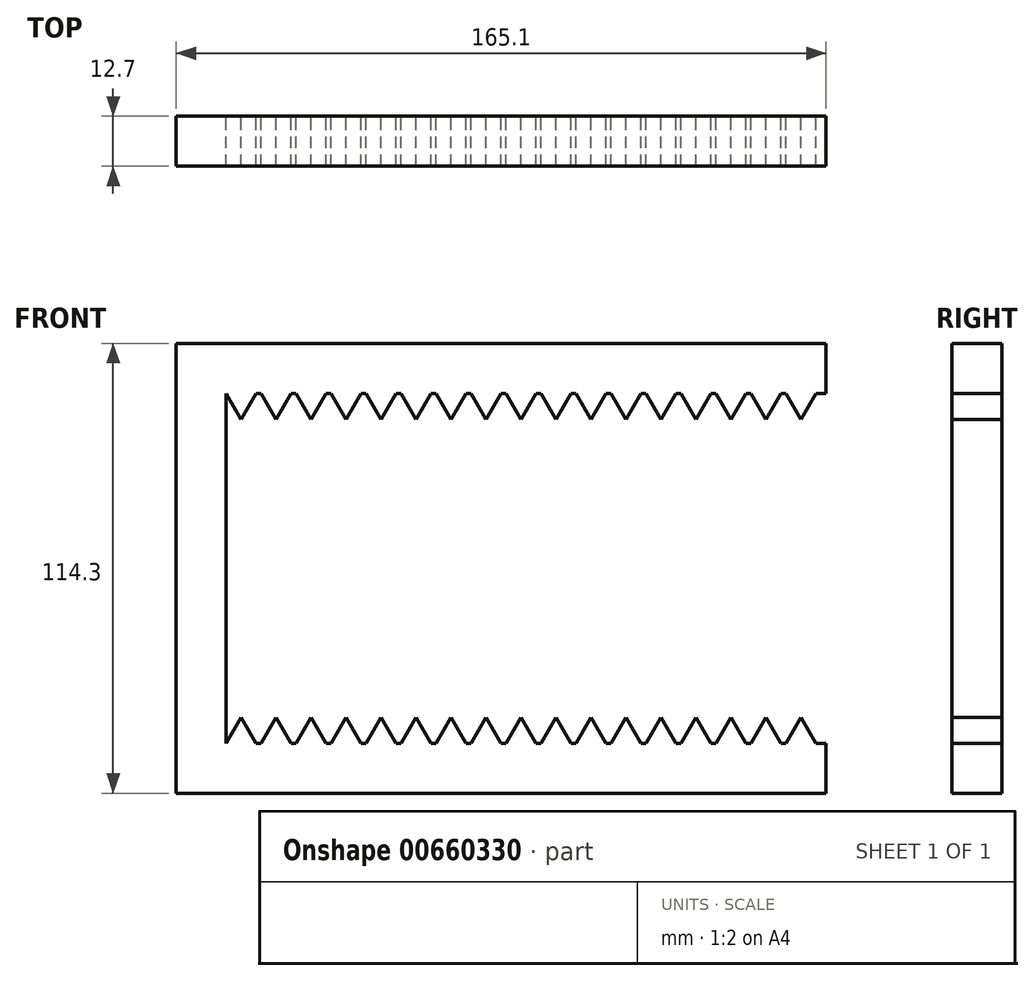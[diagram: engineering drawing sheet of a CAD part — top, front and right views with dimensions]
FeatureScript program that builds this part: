
annotation { "Feature Type Name" : "Feature", "Feature Type Description" : "" }
export const myFeature = defineFeature(function(context is Context, id is Id, definition is map)
    precondition{}
    {
        {
            var Q0;
            Q0=qCreatedBy(makeId("Front.planeOp"),FACE);
            var sketch = newSketch(context, id + "F0", { "sketchPlane" : qUnion([Q0])});
            skLineSegment(sketch, "E0", {"start": v(-49.17, 82.3) * mm, "end": v(103.23, 82.3) * mm});
            skLineSegment(sketch, "E1", {"start": v(-49.17, 82.3) * mm, "end": v(-49.17, -6.6) * mm});
            skLineSegment(sketch, "E2", {"start": v(-49.17, -6.6) * mm, "end": v(103.23, -6.6) * mm});
            skLineSegment(sketch, "E3", {"start": v(103.23, 95) * mm, "end": v(-61.87, 95) * mm});
            skLineSegment(sketch, "E4", {"start": v(-61.87, 95) * mm, "end": v(-61.87, -19.3) * mm});
            skLineSegment(sketch, "E5", {"start": v(-61.87, -19.3) * mm, "end": v(103.23, -19.3) * mm});
            skLineSegment(sketch, "E6", {"start": v(-49.17, -6.6) * mm, "end": v(-45.36, 0) * mm});
            skLineSegment(sketch, "E7", {"start": v(-45.36, 0) * mm, "end": v(-41.55, -6.6) * mm});
            skLineSegment(sketch, "E8", {"start": v(-49.17, -6.6) * mm, "end": v(-41.55, -6.6) * mm});
            skLineSegment(sketch, "E9.1.0.0", {"start": v(-36.47, 0) * mm, "end": v(-32.66, -6.6) * mm});
            skLineSegment(sketch, "E9.1.0.1", {"start": v(-40.28, -6.6) * mm, "end": v(-36.47, 0) * mm});
            skLineSegment(sketch, "E9.1.0.2", {"start": v(-40.28, -6.6) * mm, "end": v(-32.66, -6.6) * mm});
            skLineSegment(sketch, "E9.2.0.0", {"start": v(-27.58, 0) * mm, "end": v(-23.77, -6.6) * mm});
            skLineSegment(sketch, "E9.2.0.1", {"start": v(-31.4, -6.6) * mm, "end": v(-27.58, 0) * mm});
            skLineSegment(sketch, "E9.2.0.2", {"start": v(-31.4, -6.6) * mm, "end": v(-23.77, -6.6) * mm});
            skLineSegment(sketch, "E9.3.0.0", {"start": v(-18.7, 0) * mm, "end": v(-14.88, -6.6) * mm});
            skLineSegment(sketch, "E9.3.0.1", {"start": v(-22.5, -6.6) * mm, "end": v(-18.7, 0) * mm});
            skLineSegment(sketch, "E9.3.0.2", {"start": v(-22.5, -6.6) * mm, "end": v(-14.88, -6.6) * mm});
            skLineSegment(sketch, "E9.4.0.0", {"start": v(-9.8, 0) * mm, "end": v(-6, -6.6) * mm});
            skLineSegment(sketch, "E9.4.0.1", {"start": v(-13.61, -6.6) * mm, "end": v(-9.8, 0) * mm});
            skLineSegment(sketch, "E9.4.0.2", {"start": v(-13.61, -6.6) * mm, "end": v(-6, -6.6) * mm});
            skLineSegment(sketch, "E9.5.0.0", {"start": v(-0.91, 0) * mm, "end": v(2.9, -6.6) * mm});
            skLineSegment(sketch, "E9.5.0.1", {"start": v(-4.72, -6.6) * mm, "end": v(-0.91, 0) * mm});
            skLineSegment(sketch, "E9.5.0.2", {"start": v(-4.72, -6.6) * mm, "end": v(2.9, -6.6) * mm});
            skLineSegment(sketch, "E9.6.0.0", {"start": v(7.98, 0) * mm, "end": v(11.79, -6.6) * mm});
            skLineSegment(sketch, "E9.6.0.1", {"start": v(4.17, -6.6) * mm, "end": v(7.98, 0) * mm});
            skLineSegment(sketch, "E9.6.0.2", {"start": v(4.17, -6.6) * mm, "end": v(11.79, -6.6) * mm});
            skLineSegment(sketch, "E9.7.0.0", {"start": v(16.87, 0) * mm, "end": v(20.68, -6.6) * mm});
            skLineSegment(sketch, "E9.7.0.1", {"start": v(13.06, -6.6) * mm, "end": v(16.87, 0) * mm});
            skLineSegment(sketch, "E9.7.0.2", {"start": v(13.06, -6.6) * mm, "end": v(20.68, -6.6) * mm});
            skLineSegment(sketch, "E9.8.0.0", {"start": v(25.76, 0) * mm, "end": v(29.57, -6.6) * mm});
            skLineSegment(sketch, "E9.8.0.1", {"start": v(21.95, -6.6) * mm, "end": v(25.76, 0) * mm});
            skLineSegment(sketch, "E9.8.0.2", {"start": v(21.95, -6.6) * mm, "end": v(29.57, -6.6) * mm});
            skLineSegment(sketch, "E9.9.0.0", {"start": v(34.65, 0) * mm, "end": v(38.46, -6.6) * mm});
            skLineSegment(sketch, "E9.9.0.1", {"start": v(30.84, -6.6) * mm, "end": v(34.65, 0) * mm});
            skLineSegment(sketch, "E9.9.0.2", {"start": v(30.84, -6.6) * mm, "end": v(38.46, -6.6) * mm});
            skLineSegment(sketch, "E9.10.0.0", {"start": v(43.54, 0) * mm, "end": v(47.35, -6.6) * mm});
            skLineSegment(sketch, "E9.10.0.1", {"start": v(39.73, -6.6) * mm, "end": v(43.54, 0) * mm});
            skLineSegment(sketch, "E9.10.0.2", {"start": v(39.73, -6.6) * mm, "end": v(47.35, -6.6) * mm});
            skLineSegment(sketch, "E9.11.0.0", {"start": v(52.43, 0) * mm, "end": v(56.24, -6.6) * mm});
            skLineSegment(sketch, "E9.11.0.1", {"start": v(48.62, -6.6) * mm, "end": v(52.43, 0) * mm});
            skLineSegment(sketch, "E9.11.0.2", {"start": v(48.62, -6.6) * mm, "end": v(56.24, -6.6) * mm});
            skLineSegment(sketch, "E9.12.0.0", {"start": v(61.32, 0) * mm, "end": v(65.13, -6.6) * mm});
            skLineSegment(sketch, "E9.12.0.1", {"start": v(57.5, -6.6) * mm, "end": v(61.32, 0) * mm});
            skLineSegment(sketch, "E9.12.0.2", {"start": v(57.5, -6.6) * mm, "end": v(65.13, -6.6) * mm});
            skLineSegment(sketch, "E9.13.0.0", {"start": v(70.2, 0) * mm, "end": v(74.02, -6.6) * mm});
            skLineSegment(sketch, "E9.13.0.1", {"start": v(66.4, -6.6) * mm, "end": v(70.2, 0) * mm});
            skLineSegment(sketch, "E9.13.0.2", {"start": v(66.4, -6.6) * mm, "end": v(74.02, -6.6) * mm});
            skLineSegment(sketch, "E9.direction1", {"start": v(-41.55, -6.6) * mm, "end": v(-32.66, -6.6) * mm, "construction": true});
            skLineSegment(sketch, "E10", {"start": v(-49.17, 82.3) * mm, "end": v(-41.55, 82.3) * mm});
            skLineSegment(sketch, "E11", {"start": v(-41.55, 82.3) * mm, "end": v(-45.36, 75.7) * mm});
            skLineSegment(sketch, "E12", {"start": v(-45.36, 75.7) * mm, "end": v(-49.17, 82.3) * mm});
            skLineSegment(sketch, "E13", {"start": v(-41.55, 82.3) * mm, "end": v(-49.17, 82.3) * mm});
            skLineSegment(sketch, "E14.1.0.0", {"start": v(-32.66, 82.3) * mm, "end": v(-36.47, 75.7) * mm});
            skLineSegment(sketch, "E14.1.0.1", {"start": v(-36.47, 75.7) * mm, "end": v(-40.28, 82.3) * mm});
            skLineSegment(sketch, "E14.1.0.2", {"start": v(-32.66, 82.3) * mm, "end": v(-40.28, 82.3) * mm});
            skLineSegment(sketch, "E14.2.0.0", {"start": v(-23.77, 82.3) * mm, "end": v(-27.58, 75.7) * mm});
            skLineSegment(sketch, "E14.2.0.1", {"start": v(-27.58, 75.7) * mm, "end": v(-31.4, 82.3) * mm});
            skLineSegment(sketch, "E14.2.0.2", {"start": v(-23.77, 82.3) * mm, "end": v(-31.4, 82.3) * mm});
            skLineSegment(sketch, "E14.3.0.0", {"start": v(-14.88, 82.3) * mm, "end": v(-18.7, 75.7) * mm});
            skLineSegment(sketch, "E14.3.0.1", {"start": v(-18.7, 75.7) * mm, "end": v(-22.5, 82.3) * mm});
            skLineSegment(sketch, "E14.3.0.2", {"start": v(-14.88, 82.3) * mm, "end": v(-22.5, 82.3) * mm});
            skLineSegment(sketch, "E14.4.0.0", {"start": v(-6, 82.3) * mm, "end": v(-9.8, 75.7) * mm});
            skLineSegment(sketch, "E14.4.0.1", {"start": v(-9.8, 75.7) * mm, "end": v(-13.61, 82.3) * mm});
            skLineSegment(sketch, "E14.4.0.2", {"start": v(-6, 82.3) * mm, "end": v(-13.61, 82.3) * mm});
            skLineSegment(sketch, "E14.5.0.0", {"start": v(2.9, 82.3) * mm, "end": v(-0.91, 75.7) * mm});
            skLineSegment(sketch, "E14.5.0.1", {"start": v(-0.91, 75.7) * mm, "end": v(-4.72, 82.3) * mm});
            skLineSegment(sketch, "E14.5.0.2", {"start": v(2.9, 82.3) * mm, "end": v(-4.72, 82.3) * mm});
            skLineSegment(sketch, "E14.6.0.0", {"start": v(11.79, 82.3) * mm, "end": v(7.98, 75.7) * mm});
            skLineSegment(sketch, "E14.6.0.1", {"start": v(7.98, 75.7) * mm, "end": v(4.17, 82.3) * mm});
            skLineSegment(sketch, "E14.6.0.2", {"start": v(11.79, 82.3) * mm, "end": v(4.17, 82.3) * mm});
            skLineSegment(sketch, "E14.7.0.0", {"start": v(20.68, 82.3) * mm, "end": v(16.87, 75.7) * mm});
            skLineSegment(sketch, "E14.7.0.1", {"start": v(16.87, 75.7) * mm, "end": v(13.06, 82.3) * mm});
            skLineSegment(sketch, "E14.7.0.2", {"start": v(20.68, 82.3) * mm, "end": v(13.06, 82.3) * mm});
            skLineSegment(sketch, "E14.8.0.0", {"start": v(29.57, 82.3) * mm, "end": v(25.76, 75.7) * mm});
            skLineSegment(sketch, "E14.8.0.1", {"start": v(25.76, 75.7) * mm, "end": v(21.95, 82.3) * mm});
            skLineSegment(sketch, "E14.8.0.2", {"start": v(29.57, 82.3) * mm, "end": v(21.95, 82.3) * mm});
            skLineSegment(sketch, "E14.9.0.0", {"start": v(38.46, 82.3) * mm, "end": v(34.65, 75.7) * mm});
            skLineSegment(sketch, "E14.9.0.1", {"start": v(34.65, 75.7) * mm, "end": v(30.84, 82.3) * mm});
            skLineSegment(sketch, "E14.9.0.2", {"start": v(38.46, 82.3) * mm, "end": v(30.84, 82.3) * mm});
            skLineSegment(sketch, "E14.direction1", {"start": v(-45.36, 75.7) * mm, "end": v(-36.47, 75.7) * mm, "construction": true});
            skLineSegment(sketch, "E15.0.10.0", {"start": v(47.35, 82.3) * mm, "end": v(43.54, 75.7) * mm});
            skLineSegment(sketch, "E15.3.10.0", {"start": v(43.54, 75.7) * mm, "end": v(39.73, 82.3) * mm});
            skLineSegment(sketch, "E15.6.10.0", {"start": v(47.35, 82.3) * mm, "end": v(39.73, 82.3) * mm});
            skLineSegment(sketch, "E15.0.11.0", {"start": v(56.24, 82.3) * mm, "end": v(52.43, 75.7) * mm});
            skLineSegment(sketch, "E15.3.11.0", {"start": v(52.43, 75.7) * mm, "end": v(48.62, 82.3) * mm});
            skLineSegment(sketch, "E15.6.11.0", {"start": v(56.24, 82.3) * mm, "end": v(48.62, 82.3) * mm});
            skLineSegment(sketch, "E15.0.12.0", {"start": v(65.13, 82.3) * mm, "end": v(61.32, 75.7) * mm});
            skLineSegment(sketch, "E15.3.12.0", {"start": v(61.32, 75.7) * mm, "end": v(57.5, 82.3) * mm});
            skLineSegment(sketch, "E15.6.12.0", {"start": v(65.13, 82.3) * mm, "end": v(57.5, 82.3) * mm});
            skLineSegment(sketch, "E15.0.13.0", {"start": v(74.02, 82.3) * mm, "end": v(70.2, 75.7) * mm});
            skLineSegment(sketch, "E15.3.13.0", {"start": v(70.2, 75.7) * mm, "end": v(66.4, 82.3) * mm});
            skLineSegment(sketch, "E15.6.13.0", {"start": v(74.02, 82.3) * mm, "end": v(66.4, 82.3) * mm});
            skLineSegment(sketch, "E16", {"start": v(74.02, 82.3) * mm, "end": v(103.23, 82.3) * mm});
            skLineSegment(sketch, "E17", {"start": v(81.13, -19.3) * mm, "end": v(103.23, -19.3) * mm});
            skLineSegment(sketch, "E18", {"start": v(103.23, -6.6) * mm, "end": v(103.23, -19.3) * mm});
            skLineSegment(sketch, "E19.1.0.0", {"start": v(79.1, 0) * mm, "end": v(82.9, -6.6) * mm});
            skLineSegment(sketch, "E19.1.0.1", {"start": v(75.29, -6.6) * mm, "end": v(79.1, 0) * mm});
            skLineSegment(sketch, "E19.2.0.0", {"start": v(87.99, 0) * mm, "end": v(91.8, -6.6) * mm});
            skLineSegment(sketch, "E19.2.0.1", {"start": v(84.18, -6.6) * mm, "end": v(87.99, 0) * mm});
            skLineSegment(sketch, "E19.direction1", {"start": v(74.02, -6.6) * mm, "end": v(82.9, -6.6) * mm, "construction": true});
            skLineSegment(sketch, "E20.1.0.0", {"start": v(79.1, 75.7) * mm, "end": v(75.29, 82.3) * mm});
            skLineSegment(sketch, "E20.1.0.1", {"start": v(82.9, 82.3) * mm, "end": v(79.1, 75.7) * mm});
            skLineSegment(sketch, "E20.2.0.0", {"start": v(87.99, 75.7) * mm, "end": v(84.18, 82.3) * mm});
            skLineSegment(sketch, "E20.2.0.1", {"start": v(91.8, 82.3) * mm, "end": v(87.99, 75.7) * mm});
            skLineSegment(sketch, "E20.direction1", {"start": v(70.2, 75.7) * mm, "end": v(79.1, 75.7) * mm, "construction": true});
            skLineSegment(sketch, "E21.1.0.0", {"start": v(96.88, 0) * mm, "end": v(100.69, -6.6) * mm});
            skLineSegment(sketch, "E21.1.0.1", {"start": v(93.07, -6.6) * mm, "end": v(96.88, 0) * mm});
            skLineSegment(sketch, "E21.direction1", {"start": v(91.8, -6.6) * mm, "end": v(100.69, -6.6) * mm, "construction": true});
            skLineSegment(sketch, "E22.1.0.0", {"start": v(100.69, 82.3) * mm, "end": v(96.88, 75.7) * mm});
            skLineSegment(sketch, "E22.1.0.1", {"start": v(96.88, 75.7) * mm, "end": v(93.07, 82.3) * mm});
            skLineSegment(sketch, "E22.direction1", {"start": v(87.99, 75.7) * mm, "end": v(96.88, 75.7) * mm, "construction": true});
            skLineSegment(sketch, "E23", {"start": v(103.23, 95) * mm, "end": v(103.23, 82.3) * mm});
            skSolve(sketch);
        }
        {
            var Q0;
            Q0 = qSketchRegion(id + "F0", true);
            extrude(context, id + "F1", {"entities" : qUnion([Q0]), "depth" : 12.7 * mm, "offsetDistance" : 25.4 * mm});
        }
    });
